# Revit family: EC2N-LED
name_source: partatom
category: Lighting Fixtures
revit_build: Autodesk Revit 2014 (Build: 20130308_1515(x64)
units: mm (PartAtom-declared; Revit-internal decimal feet)

## types (1)
- EC2N-LED
    Apparent Load = 55 VA
    Assembly Code = D5020200
    Color Filter = 16777215
    Connector Description = Lighting Connector
    Default Elevation = 1219.2 mm  [stored 4 ft]
    Description = The Eclipse II is a Zone 2 LED well-glass up to 15640lm lumens. Utilising the very latest LED technology this 120,000 hour, highly Energy Efficient  luminaire has been designed to make installation quick and simple. It has a lightweight corrosion resistant aluminium body, heat resistant glass and stainless steel fasteners. It has been tested to IP66 and is suitable for use in harsh environments. The lamp and gear chambers are separated for easy maintenance and require no special cable glands. The luminaire also features a swing barrel nut system. This allows prior installation and wiring of the mounting base without the need to support the body and lamps.
    Dimming Lamp Color Temperature Shift = <None>
    Emit Shape Visible in Rendering = No
    Emit from Circle Diameter = 50 mm  [stored 0.164042 ft]
    Features = Instant on crisp white light output.
Highly Energy Efficient.
120,000 maintenance free hours at 25°C.
Lower power consumption than HID lamps.
Low temperature applications to -40°C.
    Fixture distribution = Direct
    Glass = Hubbell - Glass
    Height = 535 mm
    Housing Material = Paint- Hubbell- Yellow
    IP Rating = IP66/67
    Inner Length = 200 mm  [stored 0.656168 ft]
    Lamp = LED
    Length = 245 mm  [stored 0.803806 ft]
    Load Classification = Lighting
    Manufacturer = Chalmit
    Model = EC2N-LED
    Mounting = Paint - Hubbell - Light Silver
    Photometric Web File = CHL_EC2N_06L_LE.ies
    Power Factor = 1
    Product Documentation Link = https://hubbellcdn.com
    Product Link = https://www.hubbell.com
    Reflector Finish = Hubbell - White Glass
    Tilt Angle = 90.00°
    URL = https://www.hubbell.com
    Voltage = 120 V
    Warranty = 5 years Warranty
    Wattage Comments = 55W
    Watts = 55 W
    Width = 280 mm  [stored 0.918635 ft]
    Wings = Paint - Hubbell - Light Silver

note: [stored X ft] marks values corroborated as IEEE doubles in the binary element streams (Revit-internal decimal feet)

## geometry (parser evidence)
native form markers: Sweep x4
no freeform markers — native parametric forms only
